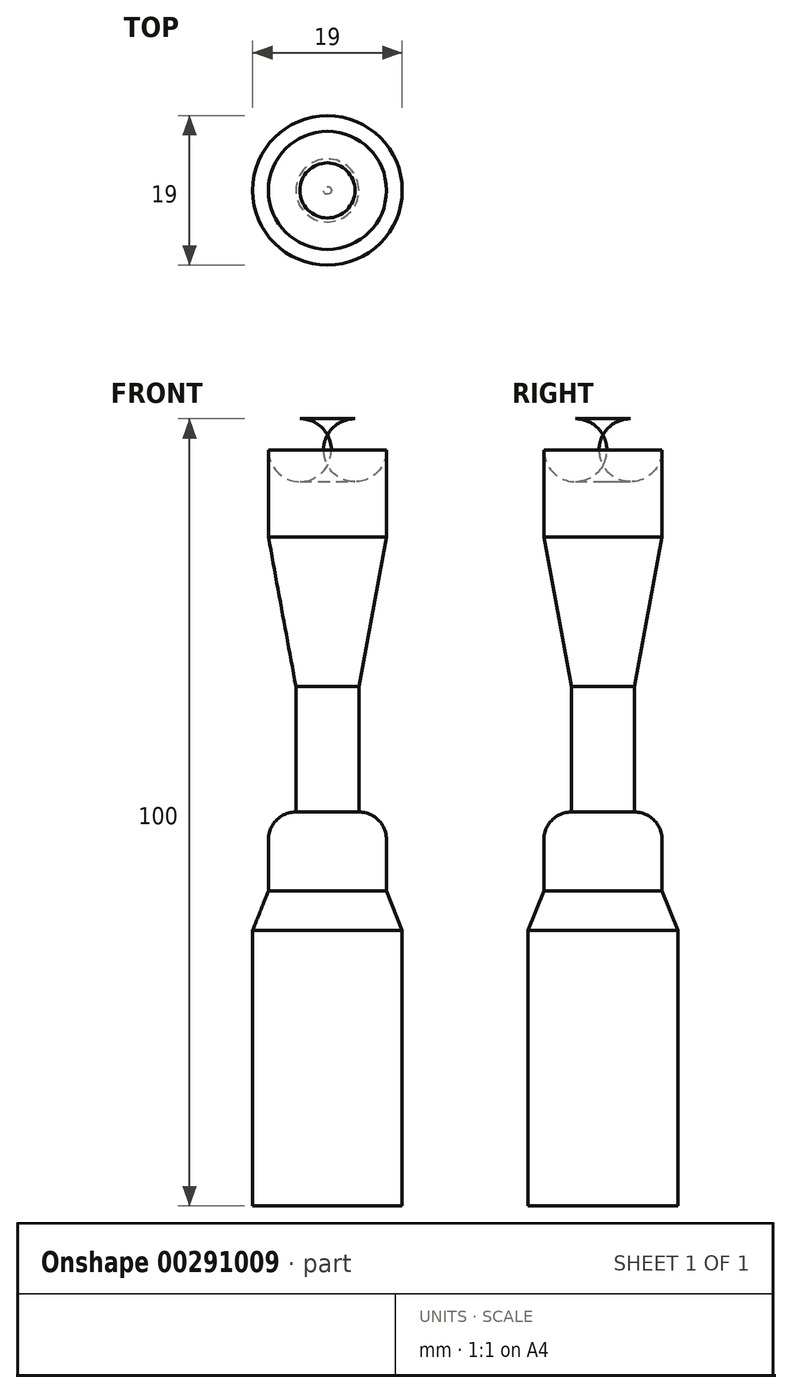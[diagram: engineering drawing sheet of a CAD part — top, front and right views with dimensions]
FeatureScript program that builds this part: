
annotation { "Feature Type Name" : "Feature", "Feature Type Description" : "" }
export const myFeature = defineFeature(function(context is Context, id is Id, definition is map)
    precondition{}
    {
        {
            var Q0;
            Q0=qCreatedBy(makeId("Front.planeOp"),FACE);
            var sketch = newSketch(context, id + "F0", { "sketchPlane" : qUnion([Q0])});
            skLineSegment(sketch, "E0", {"start": v(7.5, -4) * mm, "end": v(7.5, -15) * mm});
            skLineSegment(sketch, "E1", {"start": v(7.5, -15) * mm, "end": v(4, -34) * mm});
            skLineSegment(sketch, "E2", {"start": v(4, -34) * mm, "end": v(4, -49.97) * mm});
            skArc(sketch, "E3", {"start": v(7.5, -53.47) * mm, "mid": v(6.47, -51) * mm, "end": v(4, -49.97) * mm});
            skLineSegment(sketch, "E4", {"start": v(7.5, -53.47) * mm, "end": v(7.5, -60) * mm});
            skLineSegment(sketch, "E5", {"start": v(7.5, -60) * mm, "end": v(9.5, -65) * mm});
            skLineSegment(sketch, "E6", {"start": v(9.5, -65) * mm, "end": v(9.5, -100) * mm});
            skLineSegment(sketch, "E7", {"start": v(9.5, -100) * mm, "end": v(0, -100) * mm});
            skLineSegment(sketch, "E8", {"start": v(0, -100) * mm, "end": v(0, 0) * mm});
            skLineSegment(sketch, "E9", {"start": v(0, 0) * mm, "end": v(3.5, 0) * mm});
            skArc(sketch, "E10", {"start": v(7.5, -4) * mm, "mid": v(6.33, -1.17) * mm, "end": v(3.5, 0) * mm});
            skSolve(sketch);
        }
        {
            var Q0;
            Q0=makeQuery(id+"F0.imprint","IMPRINT",FACE,{"disambiguationData":[TD([[makeQuery(id+"F0.imprint","IMPRINT",EDGE,{"derivedFrom":sQuery(id+"F0.wireOp",EDGE,"E0")}),-1.0]])]});
            var Q1;
            Q1=sQuery(id+"F0.wireOp",EDGE,"E8");
            revolve(context, id + "F1", {"entities" : qUnion([Q0]), "axis" : qUnion([Q1]), "revolveType" : RevolveType.FULL});
        }
    });
